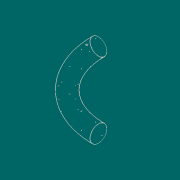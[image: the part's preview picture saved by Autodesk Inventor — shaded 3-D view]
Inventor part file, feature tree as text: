
AUTODESK INVENTOR PART (.ipt)
format: ipt  version: 2017.3 (Build 213257000, 257)  size: 390,144 bytes
history: native  units: in
note: dims shown in document units (in); Inventor stores cm internally (conversion verified against a paired STEP export)
features: plane x9, pattern_circular x7, other x5, hole x3, chamfer x2, sketch x2, revolve x1, split x1, extrude x1
ambient origin geometry x8: Origin, YZ Plane, XZ Plane, XY Plane, X Axis, Y Axis, Z Axis, Center Point
bodies: Solid1 (feature_tree)
feature tree (31):
  revolve  "Revolution1"  [1 undecoded]
  chamfer  "Chamfer3"  Angle=90.0deg  [1 undecoded]
  chamfer  "Chamfer4"  Distance=0.4375in
  plane  "Work Plane1"
  sketch  "Sketch4"  dims[d2=160.0in d3=90.0deg d14=0.4375in d15=0.125in d16=0.2577in d17=0.4375in d18=0.125in d19=0.2577in d20=18.01in d21=160.0in d22=27.2835in d23=4.125in d24=160.0in d25=6.0in d26=0.0148in d27=15.0deg d28=2.5625in d29=0.75in d30=0.375in d31=0.25in d32=0.5635in d33=1.0in d34=0.8108in d35=1.0in d36=0.0in d37=0.891in d38=0.553in d39=0.0246in d40=0.897in d41=0.375in d42=0.25in d43=0.5635in d44=0.91in d45=0.8108in d46=0.891in d47=0.553in d48=0.0246in d49=0.897in d50=0.375in d51=0.25in d52=0.5635in d53=0.91in d54=0.8108in d55=0.0148in d56=-160.0in d57=15.0deg d58=-160.0in d59=1.1811in d60=135.0deg d62=0.7874in d63=180.0deg d65=0.7874in d66=60.0deg d68=0.7874in d69=30.0deg d71=0.0675in d72=0.0675in d73=-160.0in d74=0.2944in d75=-160.0in d76=0.7874in d77=0.2944in d79=0.7874in d80=360.0deg d82=0.7874in d83=0.3827in]
  hole  "Hole1"  [1 undecoded]
  split  "Split1"
  other  "Work Axis3"
  hole  "Hole2"  [1 undecoded]
  hole  "Hole3"  [1 undecoded]
  plane  "Work Plane2"
  other  "Work Axis1"
  other  "Work Axis2"
  pattern_circular  "Circular Pattern1"  [2 undecoded]
  pattern_circular  "Circular Pattern2"  [2 undecoded]
  pattern_circular  "Circular Pattern3"  [2 undecoded]
  pattern_circular  "Circular Pattern4"  [2 undecoded]
  pattern_circular  "Circular Pattern7"  [2 undecoded]
  other  "Work Axis4"
  pattern_circular  "Circular Pattern5"  [2 undecoded]
  pattern_circular  "Circular Pattern6"  [2 undecoded]
  sketch  "Sketch1"  dims[d0=36.0in d1=35.0in]
  other  "Srf1"
  plane  "Work Plane3"
  plane  "Work Plane4"
  plane  "Work Plane5"
  plane  "Work Plane6"
  plane  "Work Plane7"
  plane  "Work Plane8"
  plane  "Work Plane9"
  extrude  "ExtrusionSrf1"  TaperAngle=15.0deg  [1 undecoded]
note: 20 required parameter values undecoded (feature->parameter linkage not recoverable at this tier; creation-order binding heuristic only, values carry confidence <= 0.55)